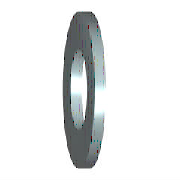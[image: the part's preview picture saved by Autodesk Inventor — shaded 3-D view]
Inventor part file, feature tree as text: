
AUTODESK INVENTOR PART (.ipt)
format: ipt  version: 2017 (Build 210142000, 142)  size: 104,448 bytes
history: native  units: mm (DEFAULTED — no unit token found)
features: other x1, plane x1, sketch x1
ambient origin geometry x7: Origin, YZ Plane, XY Plane, X Axis, Y Axis, Z Axis, Center Point
bodies: Solid1 (feature_tree), Body (feature_tree)
feature tree (3):
  other  "Work Axis1"
  plane  "Work Plane1"
  sketch  "Sketch"  dims[d0=5.3mm d1=15.0mm d2=1.2mm d3=0.0mm d4=0.0mm d5=0.0mm d6=0.0mm d7=0.0mm]
